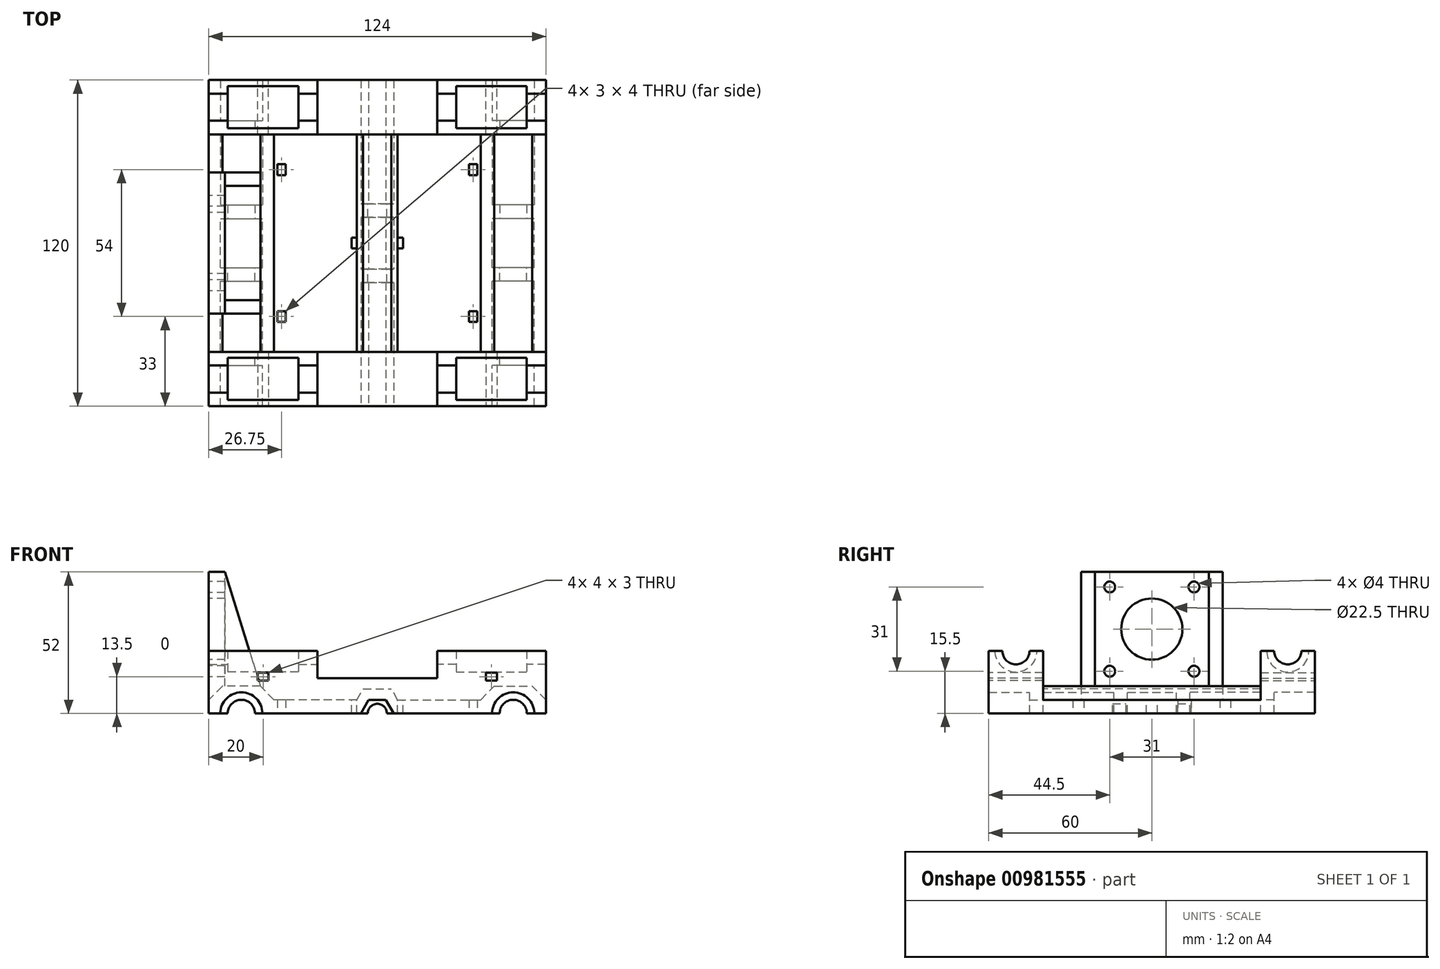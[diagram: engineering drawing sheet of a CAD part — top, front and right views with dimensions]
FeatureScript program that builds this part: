
annotation { "Feature Type Name" : "Feature", "Feature Type Description" : "" }
export const myFeature = defineFeature(function(context is Context, id is Id, definition is map)
    precondition{}
    {
        {
            var Q0;
            Q0=qCreatedBy(makeId("Front.planeOp"),FACE);
            var sketch = newSketch(context, id + "F0", { "sketchPlane" : qUnion([Q0])});
            skLineSegment(sketch, "E0", {"start": v(0, 0) * mm, "end": v(-42.25, 0) * mm});
            skArc(sketch, "E1", {"start": v(-42.25, 0) * mm, "mid": v(-50, 7.75) * mm, "end": v(-57.75, 0) * mm});
            skLineSegment(sketch, "E2", {"start": v(-57.75, 0) * mm, "end": v(-62, 0) * mm});
            skLineSegment(sketch, "E3", {"start": v(-43, 10) * mm, "end": v(-38, 5) * mm});
            skLineSegment(sketch, "E4", {"start": v(-38, 5) * mm, "end": v(0, 5) * mm});
            skLineSegment(sketch, "E5", {"start": v(-57, 10) * mm, "end": v(-43, 10) * mm});
            skLineSegment(sketch, "E6", {"start": v(-57, 10) * mm, "end": v(-62, 5) * mm});
            skLineSegment(sketch, "E7", {"start": v(-62, 5) * mm, "end": v(-62, 0) * mm});
            skLineSegment(sketch, "E8", {"start": v(0, 0) * mm, "end": v(0, 5) * mm});
            skSolve(sketch);
        }
        {
            var Q0;
            Q0=makeQuery(id+"F0.imprint","IMPRINT",FACE,{"disambiguationData":[TD([[makeQuery(id+"F0.imprint","IMPRINT",EDGE,{"derivedFrom":sQuery(id+"F0.wireOp",EDGE,"E0")}),-1.0]])]});
            extrude(context, id + "F1", {"entities" : qUnion([Q0]), "endBound" : BoundingType.SYMMETRIC, "depth" : 120 * mm, "offsetDistance" : 25 * mm});
        }
        {
            var Q0;
            Q0=makeQuery(id+"F1.opExtrude","SWEPT_BODY",BODY,{"disambiguationData":[OSD([sQuery(id+"F0.wireOp",EDGE,"E0"),sQuery(id+"F0.wireOp",EDGE,"E1"),sQuery(id+"F0.wireOp",EDGE,"E2"),sQuery(id+"F0.wireOp",EDGE,"E3"),sQuery(id+"F0.wireOp",EDGE,"E4"),sQuery(id+"F0.wireOp",EDGE,"E5"),sQuery(id+"F0.wireOp",EDGE,"E6"),sQuery(id+"F0.wireOp",EDGE,"E7"),sQuery(id+"F0.wireOp",EDGE,"E8")])]});
            var Q1;
            Q1=qCreatedBy(makeId("Right.planeOp"),FACE);
            mirror(context, id + "F2", {"operationType" : NewBodyOperationType.ADD, "entities" : qUnion([Q0]), "mirrorPlane" : qUnion([Q1])});
        }
        {
            var Q0;
            {var subQ0=makeQuery(id+"F1.opExtrude","CAP_FACE",FACE,{"disambiguationData":[OSD([sQuery(id+"F0.wireOp",EDGE,"E0"),sQuery(id+"F0.wireOp",EDGE,"E1"),sQuery(id+"F0.wireOp",EDGE,"E2"),sQuery(id+"F0.wireOp",EDGE,"E3"),sQuery(id+"F0.wireOp",EDGE,"E4"),sQuery(id+"F0.wireOp",EDGE,"E5"),sQuery(id+"F0.wireOp",EDGE,"E6"),sQuery(id+"F0.wireOp",EDGE,"E7"),sQuery(id+"F0.wireOp",EDGE,"E8")])],"isStart":false});Q0=makeQuery(id+"F2.boolean.opBoolean","MERGE",FACE,{"derivedFrom":[subQ0,makeQuery(id+"F2.opPattern","COPY",FACE,{"derivedFrom":subQ0,"instanceName":"1"})]});}
            var sketch = newSketch(context, id + "F3", { "sketchPlane" : qUnion([Q0])});
            skCircle(sketch, "E9.cCircle", {"center": v(0, 0) * mm, "radius": 5.25 * mm, "construction": true});
            skLineSegment(sketch, "E9.0", {"start": v(-3.03, 5.25) * mm, "end": v(3.03, 5.25) * mm});
            skLineSegment(sketch, "E9.1", {"start": v(3.03, 5.25) * mm, "end": v(6.06, 0) * mm});
            skLineSegment(sketch, "E9.2", {"start": v(6.06, 0) * mm, "end": v(3.03, -5.25) * mm});
            skLineSegment(sketch, "E9.3", {"start": v(3.03, -5.25) * mm, "end": v(-3.03, -5.25) * mm});
            skLineSegment(sketch, "E9.4", {"start": v(-3.03, -5.25) * mm, "end": v(-6.06, 0) * mm});
            skLineSegment(sketch, "E9.5", {"start": v(-6.06, 0) * mm, "end": v(-3.03, 5.25) * mm});
            skPoint(sketch, "E9.0.midPoint", {"position": v(0, 5.25) * mm});
            skCircle(sketch, "E10.cCircle", {"center": v(0, 0) * mm, "radius": 9 * mm, "construction": true});
            skLineSegment(sketch, "E10.0", {"start": v(-5.2, 9) * mm, "end": v(5.2, 9) * mm});
            skLineSegment(sketch, "E10.1", {"start": v(5.2, 9) * mm, "end": v(10.4, 0) * mm});
            skLineSegment(sketch, "E10.2", {"start": v(10.4, 0) * mm, "end": v(5.2, -9) * mm});
            skLineSegment(sketch, "E10.3", {"start": v(5.2, -9) * mm, "end": v(-5.2, -9) * mm});
            skLineSegment(sketch, "E10.4", {"start": v(-5.2, -9) * mm, "end": v(-10.4, 0) * mm});
            skLineSegment(sketch, "E10.5", {"start": v(-10.4, 0) * mm, "end": v(-5.2, 9) * mm});
            skPoint(sketch, "E10.0.midPoint", {"position": v(0, 9) * mm});
            skLineSegment(sketch, "E11", {"start": v(-10.4, 0) * mm, "end": v(10.4, 0) * mm});
            skSolve(sketch);
        }
        {
            var Q0;
            {var subQ0=sQuery(id+"F3.wireOp",EDGE,"E11");var subQ1=sQuery(id+"F3.wireOp",EDGE,"E9.5");var subQ2=makeQuery(id+"F3.imprint","INTERSECT",VERTEX,{"derivedFrom":[sQuery(id+"F3.wireOp",EDGE,"E9.4"),subQ1,subQ0]});Q0=makeQuery(id+"F3.imprint","IMPRINT",FACE,{"disambiguationData":[TD([[makeQuery(id+"F3.imprint","IMPRINT",EDGE,{"disambiguationData":[TD([[subQ2,-1.0]])],"derivedFrom":subQ1}),1.0]])]});}
            var Q1;
            {var subQ2=sQuery(id+"F3.wireOp",EDGE,"E9.0");Q1=makeQuery(id+"F3.imprint","IMPRINT",FACE,{"disambiguationData":[TD([[makeQuery(id+"F3.imprint","IMPRINT",EDGE,{"derivedFrom":subQ2}),1.0]])]});}
            var Q2;
            {var subQ0=sQuery(id+"F3.wireOp",EDGE,"E11");var subQ1=sQuery(id+"F3.wireOp",EDGE,"E9.1");var subQ2=makeQuery(id+"F3.imprint","INTERSECT",VERTEX,{"derivedFrom":[subQ1,sQuery(id+"F3.wireOp",EDGE,"E9.2"),subQ0]});Q2=makeQuery(id+"F3.imprint","IMPRINT",FACE,{"disambiguationData":[TD([[makeQuery(id+"F3.imprint","IMPRINT",EDGE,{"disambiguationData":[TD([[subQ2,1.0]])],"derivedFrom":subQ1}),1.0]])]});}
            var Q3;
            {var subQ0=sQuery(id+"F3.wireOp",EDGE,"E9.0");Q3=makeQuery(id+"F3.imprint","IMPRINT",FACE,{"disambiguationData":[TD([[makeQuery(id+"F3.imprint","IMPRINT",EDGE,{"derivedFrom":subQ0}),-1.0]])]});}
            var Q4;
            {var subQ0=makeQuery(id+"F1.opExtrude","CAP_FACE",FACE,{"disambiguationData":[OSD([sQuery(id+"F0.wireOp",EDGE,"E0"),sQuery(id+"F0.wireOp",EDGE,"E1"),sQuery(id+"F0.wireOp",EDGE,"E2"),sQuery(id+"F0.wireOp",EDGE,"E3"),sQuery(id+"F0.wireOp",EDGE,"E4"),sQuery(id+"F0.wireOp",EDGE,"E5"),sQuery(id+"F0.wireOp",EDGE,"E6"),sQuery(id+"F0.wireOp",EDGE,"E7"),sQuery(id+"F0.wireOp",EDGE,"E8")])],"isStart":true});Q4=makeQuery(id+"F2.boolean.opBoolean","MERGE",FACE,{"derivedFrom":[subQ0,makeQuery(id+"F2.opPattern","COPY",FACE,{"derivedFrom":subQ0,"instanceName":"1"})]});}
            extrude(context, id + "F4", {"entities" : qUnion([Q0, Q1, Q2, Q3]), "operationType" : NewBodyOperationType.ADD, "endBound" : BoundingType.UP_TO_SURFACE, "oppositeDirection" : true, "depth" : 123.9 * mm, "endBoundEntityFace" : qUnion([Q4]), "offsetDistance" : 25 * mm});
        }
        {
            var Q0;
            {var subQ0=sQuery(id+"F3.wireOp",EDGE,"E11");var subQ1=sQuery(id+"F3.wireOp",EDGE,"E9.1");var subQ2=makeQuery(id+"F3.imprint","INTERSECT",VERTEX,{"derivedFrom":[subQ1,sQuery(id+"F3.wireOp",EDGE,"E9.2"),subQ0]});Q0=makeQuery(id+"F3.imprint","IMPRINT",FACE,{"disambiguationData":[TD([[makeQuery(id+"F3.imprint","IMPRINT",EDGE,{"disambiguationData":[TD([[subQ2,1.0]])],"derivedFrom":subQ1}),-1.0]])]});}
            extrude(context, id + "F5", {"entities" : qUnion([Q0]), "operationType" : NewBodyOperationType.REMOVE, "endBound" : BoundingType.THROUGH_ALL, "oppositeDirection" : true, "depth" : 25 * mm, "offsetDistance" : 25 * mm});
        }
        {
            var Q0;
            Q0=makeQuery(id+"F1.opExtrude","SWEPT_FACE",FACE,{"disambiguationData":[OSD([sQuery(id+"F0.wireOp",EDGE,"E5")])]});
            var sketch = newSketch(context, id + "F6", { "sketchPlane" : qUnion([Q0])});
            skLineSegment(sketch, "E12.bottom", {"start": v(62, -40) * mm, "end": v(-62, -40) * mm});
            skLineSegment(sketch, "E12.top", {"start": v(62, -60) * mm, "end": v(-62, -60) * mm});
            skLineSegment(sketch, "E12.left", {"start": v(62, -40) * mm, "end": v(62, -60) * mm});
            skLineSegment(sketch, "E12.right", {"start": v(-62, -40) * mm, "end": v(-62, -60) * mm});
            skPoint(sketch, "E12.middle", {"position": v(0, -50) * mm});
            skSolve(sketch);
        }
        {
            var Q0;
            {var subQ0=sQuery(id+"F6.wireOp",EDGE,"E12.right");Q0=makeQuery(id+"F6.imprint","IMPRINT",FACE,{"disambiguationData":[TD([[makeQuery(id+"F6.imprint","IMPRINT",EDGE,{"derivedFrom":subQ0}),1.0]])]});}
            var Q1;
            {var subQ0=sQuery(id+"F6.wireOp",EDGE,"E12.bottom");var subQ1=sQuery(id+"F0.wireOp",EDGE,"E5");var subQ2=makeQuery(id+"F1.opExtrude","SWEPT_EDGE",EDGE,{"disambiguationData":[OSD([sQuery(id+"F0.wireOp",EDGE,"E3"),subQ1])]});var subQ3=makeQuery(id+"F6.imprint","INTERSECT",VERTEX,{"derivedFrom":[subQ2,subQ0]});Q1=makeQuery(id+"F6.imprint","IMPRINT",FACE,{"disambiguationData":[TD([[makeQuery(id+"F6.imprint","IMPRINT",EDGE,{"disambiguationData":[TD([[subQ3,-1.0]])],"derivedFrom":subQ0}),1.0]])]});}
            var Q2;
            {var subQ0=sQuery(id+"F6.wireOp",EDGE,"E12.left");Q2=makeQuery(id+"F6.imprint","IMPRINT",FACE,{"disambiguationData":[TD([[makeQuery(id+"F6.imprint","IMPRINT",EDGE,{"derivedFrom":subQ0}),-1.0]])]});}
            var Q3;
            {var subQ1=sQuery(id+"F0.wireOp",EDGE,"E5");var subQ6=makeQuery(id+"F1.opExtrude","CAP_EDGE",EDGE,{"disambiguationData":[OSD([subQ1])],"isStart":true});Q3=makeQuery(id+"F6.imprint","IMPRINT",FACE,{"disambiguationData":[TD([[makeQuery(id+"F6.imprint","IMPRINT",EDGE,{"derivedFrom":subQ6}),-1.0]])]});}
            var Q4;
            Q4=makeQuery(id+"F1.opExtrude","SWEPT_BODY",BODY,{"disambiguationData":[OSD([sQuery(id+"F0.wireOp",EDGE,"E0"),sQuery(id+"F0.wireOp",EDGE,"E1"),sQuery(id+"F0.wireOp",EDGE,"E2"),sQuery(id+"F0.wireOp",EDGE,"E3"),sQuery(id+"F0.wireOp",EDGE,"E4"),sQuery(id+"F0.wireOp",EDGE,"E5"),sQuery(id+"F0.wireOp",EDGE,"E6"),sQuery(id+"F0.wireOp",EDGE,"E7"),sQuery(id+"F0.wireOp",EDGE,"E8")])]});
            extrude(context, id + "F7", {"entities" : qUnion([Q0, Q1, Q2, Q3]), "operationType" : NewBodyOperationType.ADD, "endBound" : BoundingType.UP_TO_BODY, "oppositeDirection" : true, "depth" : 25 * mm, "endBoundEntityBody" : qUnion([Q4]), "offsetDistance" : 25 * mm});
        }
        {
            var Q0;
            Q0 = qSketchRegion(id + "F6", true);
            extrude(context, id + "F8", {"entities" : qUnion([Q0]), "operationType" : NewBodyOperationType.ADD, "depth" : 3 * mm, "offsetDistance" : 25 * mm});
        }
        {
            var Q0;
            {var subQ0=sQuery(id+"F6.wireOp",EDGE,"E12.right");Q0=makeQuery(id+"F8.boolean.opBoolean","MERGE",FACE,{"derivedFrom":[makeQuery(id+"F7.boolean.opBoolean","MERGE",FACE,{"derivedFrom":[makeQuery(id+"F1.opExtrude","SWEPT_FACE",FACE,{"disambiguationData":[OSD([sQuery(id+"F0.wireOp",EDGE,"E7")])]}),makeQuery(id+"F7.opExtrude","SWEPT_FACE",FACE,{"disambiguationData":[OSD([subQ0])]})]}),makeQuery(id+"F8.opExtrude","SWEPT_FACE",FACE,{"disambiguationData":[OSD([subQ0])]})]});}
            var sketch = newSketch(context, id + "F9", { "sketchPlane" : qUnion([Q0])});
            skLineSegment(sketch, "E13", {"start": v(50, 13) * mm, "end": v(50, 23) * mm, "construction": true});
            skArc(sketch, "E14", {"start": v(42.25, 23) * mm, "mid": v(44.52, 17.52) * mm, "end": v(50, 15.25) * mm});
            skLineSegment(sketch, "E15", {"start": v(50, 23) * mm, "end": v(40, 23) * mm, "construction": true});
            skLineSegment(sketch, "E16", {"start": v(40, 23) * mm, "end": v(40, 13) * mm});
            skLineSegment(sketch, "E17", {"start": v(42.25, 23) * mm, "end": v(40, 23) * mm});
            skLineSegment(sketch, "E18", {"start": v(50, 15.25) * mm, "end": v(50, 13) * mm});
            skLineSegment(sketch, "E19.MirrorCS", {"start": v(57.75, 23) * mm, "end": v(60, 23) * mm});
            skLineSegment(sketch, "E20.MirrorCS", {"start": v(50, 23) * mm, "end": v(60, 23) * mm, "construction": true});
            skArc(sketch, "E21.MirrorCS", {"start": v(57.75, 23) * mm, "mid": v(55.48, 17.52) * mm, "end": v(50, 15.25) * mm});
            skLineSegment(sketch, "E22.MirrorCS", {"start": v(60, 23) * mm, "end": v(60, 13) * mm});
            skLineSegment(sketch, "E23", {"start": v(40, 13) * mm, "end": v(60, 13) * mm});
            skSolve(sketch);
        }
        {
            var Q0;
            Q0 = qSketchRegion(id + "F9", true);
            extrude(context, id + "F10", {"entities" : qUnion([Q0]), "operationType" : NewBodyOperationType.ADD, "oppositeDirection" : true, "depth" : 40 * mm, "offsetDistance" : 25 * mm});
        }
        {
            var Q0;
            {var subQ0=sQuery(id+"F6.wireOp",EDGE,"E12.right");Q0=makeQuery(id+"F10.boolean.opBoolean","MERGE",FACE,{"derivedFrom":[makeQuery(id+"F8.boolean.opBoolean","MERGE",FACE,{"derivedFrom":[makeQuery(id+"F7.boolean.opBoolean","MERGE",FACE,{"derivedFrom":[makeQuery(id+"F1.opExtrude","SWEPT_FACE",FACE,{"disambiguationData":[OSD([sQuery(id+"F0.wireOp",EDGE,"E7")])]}),makeQuery(id+"F7.opExtrude","SWEPT_FACE",FACE,{"disambiguationData":[OSD([subQ0])]})]}),makeQuery(id+"F8.opExtrude","SWEPT_FACE",FACE,{"disambiguationData":[OSD([subQ0])]})]}),makeQuery(id+"F10.opExtrude","CAP_FACE",FACE,{"disambiguationData":[OSD([sQuery(id+"F9.wireOp",EDGE,"E14"),sQuery(id+"F9.wireOp",EDGE,"E16"),sQuery(id+"F9.wireOp",EDGE,"E17"),sQuery(id+"F9.wireOp",EDGE,"E21.MirrorCS"),sQuery(id+"F9.wireOp",EDGE,"E19.MirrorCS"),sQuery(id+"F9.wireOp",EDGE,"E22.MirrorCS"),sQuery(id+"F9.wireOp",EDGE,"E23")])],"isStart":true})]});}
            var sketch = newSketch(context, id + "F11", { "sketchPlane" : qUnion([Q0])});
            skLineSegment(sketch, "E24", {"start": v(42.25, 23) * mm, "end": v(57.75, 23) * mm});
            skSolve(sketch);
        }
        {
            var Q0;
            Q0=makeQuery(id+"F11.imprint","IMPRINT",FACE,{"disambiguationData":[TD([[makeQuery(id+"F11.imprint","IMPRINT",EDGE,{"derivedFrom":sQuery(id+"F11.wireOp",EDGE,"E24")}),-1.0]])]});
            extrude(context, id + "F12", {"entities" : qUnion([Q0]), "operationType" : NewBodyOperationType.ADD, "oppositeDirection" : true, "depth" : 7 * mm, "offsetDistance" : 25 * mm});
        }
        {
            var Q0;
            Q0=makeQuery(id+"F10.opExtrude","CAP_FACE",FACE,{"disambiguationData":[OSD([sQuery(id+"F9.wireOp",EDGE,"E14"),sQuery(id+"F9.wireOp",EDGE,"E16"),sQuery(id+"F9.wireOp",EDGE,"E17"),sQuery(id+"F9.wireOp",EDGE,"E21.MirrorCS"),sQuery(id+"F9.wireOp",EDGE,"E19.MirrorCS"),sQuery(id+"F9.wireOp",EDGE,"E22.MirrorCS"),sQuery(id+"F9.wireOp",EDGE,"E23")])],"isStart":false});
            var sketch = newSketch(context, id + "F13", { "sketchPlane" : qUnion([Q0])});
            skLineSegment(sketch, "E25", {"start": v(-57.75, 23) * mm, "end": v(-42.25, 23) * mm});
            skSolve(sketch);
        }
        {
            var Q0;
            Q0=makeQuery(id+"F13.imprint","IMPRINT",FACE,{"disambiguationData":[TD([[makeQuery(id+"F13.imprint","IMPRINT",EDGE,{"derivedFrom":sQuery(id+"F13.wireOp",EDGE,"E25")}),-1.0]])]});
            extrude(context, id + "F14", {"entities" : qUnion([Q0]), "operationType" : NewBodyOperationType.ADD, "oppositeDirection" : true, "depth" : 7 * mm, "offsetDistance" : 25 * mm});
        }
        {
            var Q0;
            Q0=makeQuery(id+"F12.opExtrude","CAP_FACE",FACE,{"disambiguationData":[OSD([sQuery(id+"F9.wireOp",EDGE,"E14"),sQuery(id+"F9.wireOp",EDGE,"E21.MirrorCS"),sQuery(id+"F11.wireOp",EDGE,"E24")])],"isStart":false});
            var sketch = newSketch(context, id + "F15", { "sketchPlane" : qUnion([Q0])});
            skCircle(sketch, "E26", {"center": v(-50, 23) * mm, "radius": 5 * mm});
            skSolve(sketch);
        }
        {
            var Q0;
            Q0 = qSketchRegion(id + "F15", true);
            extrude(context, id + "F16", {"entities" : qUnion([Q0]), "operationType" : NewBodyOperationType.REMOVE, "endBound" : BoundingType.SYMMETRIC, "oppositeDirection" : true, "depth" : 100 * mm, "offsetDistance" : 25 * mm});
        }
        {
            var Q0;
            {var subQ0=sQuery(id+"F0.wireOp",EDGE,"E1");var subQ8=sQuery(id+"F0.wireOp",EDGE,"E0");var subQ17=makeQuery(id+"F1.opExtrude","SWEPT_FACE",FACE,{"disambiguationData":[OSD([subQ8])]});Q0=makeQuery(id+"F5.boolean.opBoolean","SPLIT",FACE,{"disambiguationData":[TD([makeQuery(id+"F1.opExtrude","SWEPT_FACE",FACE,{"disambiguationData":[OSD([subQ0])]})])],"derivedFrom":makeQuery(id+"F2.boolean.opBoolean","MERGE",FACE,{"derivedFrom":[subQ17,makeQuery(id+"F2.opPattern","COPY",FACE,{"derivedFrom":subQ17,"instanceName":"1"})]})});}
            var sketch = newSketch(context, id + "F17", { "sketchPlane" : qUnion([Q0])});
            skLineSegment(sketch, "E27.bottom", {"start": v(-57.75, 45) * mm, "end": v(-42.25, 45) * mm});
            skLineSegment(sketch, "E27.top", {"start": v(-57.75, 40) * mm, "end": v(-42.25, 40) * mm});
            skLineSegment(sketch, "E27.left", {"start": v(-57.75, 45) * mm, "end": v(-57.75, 40) * mm});
            skLineSegment(sketch, "E27.right", {"start": v(-42.25, 45) * mm, "end": v(-42.25, 40) * mm});
            skLineSegment(sketch, "E28.bottom", {"start": v(-57.75, 14) * mm, "end": v(-42.25, 14) * mm});
            skLineSegment(sketch, "E28.top", {"start": v(-57.75, 9) * mm, "end": v(-42.25, 9) * mm});
            skLineSegment(sketch, "E28.left", {"start": v(-57.75, 14) * mm, "end": v(-57.75, 9) * mm});
            skLineSegment(sketch, "E28.right", {"start": v(-42.25, 14) * mm, "end": v(-42.25, 9) * mm});
            skSolve(sketch);
        }
        {
            var Q0;
            Q0 = qSketchRegion(id + "F17", true);
            var Q1;
            Q1=makeQuery(id+"F1.opExtrude","SWEPT_FACE",FACE,{"disambiguationData":[OSD([sQuery(id+"F0.wireOp",EDGE,"E1")])]});
            var Q2;
            Q2=makeQuery(id+"F1.opExtrude","SWEPT_BODY",BODY,{"disambiguationData":[OSD([sQuery(id+"F0.wireOp",EDGE,"E0"),sQuery(id+"F0.wireOp",EDGE,"E1"),sQuery(id+"F0.wireOp",EDGE,"E2"),sQuery(id+"F0.wireOp",EDGE,"E3"),sQuery(id+"F0.wireOp",EDGE,"E4"),sQuery(id+"F0.wireOp",EDGE,"E5"),sQuery(id+"F0.wireOp",EDGE,"E6"),sQuery(id+"F0.wireOp",EDGE,"E7"),sQuery(id+"F0.wireOp",EDGE,"E8")])]});
            extrude(context, id + "F18", {"entities" : qUnion([Q0]), "operationType" : NewBodyOperationType.ADD, "endBound" : BoundingType.UP_TO_SURFACE, "oppositeDirection" : true, "depth" : 25 * mm, "endBoundEntityFace" : qUnion([Q1]), "endBoundEntityBody" : qUnion([Q2]), "offsetDistance" : 25 * mm});
        }
        {
            var Q0;
            Q0=makeQuery(id+"F18.opExtrude","SWEPT_FACE",FACE,{"disambiguationData":[OSD([sQuery(id+"F17.wireOp",EDGE,"E28.top")])]});
            var sketch = newSketch(context, id + "F19", { "sketchPlane" : qUnion([Q0])});
            skCircle(sketch, "E29", {"center": v(50, 0) * mm, "radius": 5 * mm});
            skSolve(sketch);
        }
        {
            var Q0;
            Q0 = qSketchRegion(id + "F19", true);
            extrude(context, id + "F20", {"entities" : qUnion([Q0]), "operationType" : NewBodyOperationType.REMOVE, "endBound" : BoundingType.THROUGH_ALL, "oppositeDirection" : true, "depth" : 25 * mm, "offsetDistance" : 25 * mm});
        }
        {
            var Q0;
            {var subQ0=sQuery(id+"F6.wireOp",EDGE,"E12.top");var subQ1=sQuery(id+"F0.wireOp",EDGE,"E4");var subQ2=makeQuery(id+"F1.opExtrude","CAP_FACE",FACE,{"disambiguationData":[OSD([sQuery(id+"F0.wireOp",EDGE,"E0"),sQuery(id+"F0.wireOp",EDGE,"E1"),sQuery(id+"F0.wireOp",EDGE,"E2"),sQuery(id+"F0.wireOp",EDGE,"E3"),subQ1,sQuery(id+"F0.wireOp",EDGE,"E5"),sQuery(id+"F0.wireOp",EDGE,"E6"),sQuery(id+"F0.wireOp",EDGE,"E7"),sQuery(id+"F0.wireOp",EDGE,"E8")])],"isStart":false});Q0=makeQuery(id+"F10.boolean.opBoolean","MERGE",FACE,{"derivedFrom":[makeQuery(id+"F8.boolean.opBoolean","MERGE",FACE,{"derivedFrom":[makeQuery(id+"F7.boolean.opBoolean","MERGE",FACE,{"derivedFrom":[makeQuery(id+"F4.boolean.opBoolean","MERGE",FACE,{"derivedFrom":[makeQuery(id+"F2.boolean.opBoolean","MERGE",FACE,{"derivedFrom":[subQ2,makeQuery(id+"F2.opPattern","COPY",FACE,{"derivedFrom":subQ2,"instanceName":"1"})]}),makeQuery(id+"F4.opExtrude","CAP_FACE",FACE,{"disambiguationData":[OSD([subQ1,sQuery(id+"F3.wireOp",EDGE,"E9.1"),sQuery(id+"F3.wireOp",EDGE,"E9.5"),sQuery(id+"F3.wireOp",EDGE,"E10.0"),sQuery(id+"F3.wireOp",EDGE,"E10.1"),sQuery(id+"F3.wireOp",EDGE,"E10.5"),sQuery(id+"F3.wireOp",EDGE,"E11")])],"isStart":true})]}),makeQuery(id+"F7.opExtrude","SWEPT_FACE",FACE,{"disambiguationData":[OSD([subQ0])]})]}),makeQuery(id+"F8.opExtrude","SWEPT_FACE",FACE,{"disambiguationData":[OSD([subQ0])]})]}),makeQuery(id+"F10.opExtrude","SWEPT_FACE",FACE,{"disambiguationData":[OSD([sQuery(id+"F9.wireOp",EDGE,"E22.MirrorCS")])]})]});}
            var sketch = newSketch(context, id + "F21", { "sketchPlane" : qUnion([Q0])});
            skLineSegment(sketch, "E30", {"start": v(-42, 23) * mm, "end": v(-42, 13.5) * mm, "construction": true});
            skLineSegment(sketch, "E31.bottom", {"start": v(-40, 12) * mm, "end": v(-44, 12) * mm});
            skLineSegment(sketch, "E31.top", {"start": v(-40, 15) * mm, "end": v(-44, 15) * mm});
            skLineSegment(sketch, "E31.left", {"start": v(-40, 12) * mm, "end": v(-40, 15) * mm});
            skLineSegment(sketch, "E31.right", {"start": v(-44, 12) * mm, "end": v(-44, 15) * mm});
            skPoint(sketch, "E31.middle", {"position": v(-42, 13.5) * mm});
            skSolve(sketch);
        }
        {
            var Q0;
            Q0=makeQuery(id+"F21.imprint","IMPRINT",FACE,{"disambiguationData":[TD([[makeQuery(id+"F21.imprint","IMPRINT",EDGE,{"derivedFrom":sQuery(id+"F21.wireOp",EDGE,"E31.bottom")}),-1.0]])]});
            extrude(context, id + "F22", {"entities" : qUnion([Q0]), "operationType" : NewBodyOperationType.REMOVE, "endBound" : BoundingType.THROUGH_ALL, "oppositeDirection" : true, "depth" : 25 * mm, "offsetDistance" : 25 * mm});
        }
        {
            var Q0;
            {var subQ1=sQuery(id+"F17.wireOp",EDGE,"E28.top");var subQ2=sQuery(id+"F3.wireOp",EDGE,"E9.5");var subQ3=makeQuery(id+"F5.opExtrude","SWEPT_FACE",FACE,{"disambiguationData":[OSD([subQ2])]});var subQ16=sQuery(id+"F0.wireOp",EDGE,"E2");var subQ17=sQuery(id+"F0.wireOp",EDGE,"E1");var subQ18=sQuery(id+"F0.wireOp",EDGE,"E0");var subQ20=sQuery(id+"F17.wireOp",EDGE,"E27.top");var subQ24=sQuery(id+"F17.wireOp",EDGE,"E28.bottom");var subQ26=makeQuery(id+"F1.opExtrude","SWEPT_FACE",FACE,{"disambiguationData":[OSD([subQ17])]});var subQ27=sQuery(id+"F17.wireOp",EDGE,"E27.bottom");var subQ28=makeQuery(id+"F1.opExtrude","SWEPT_FACE",FACE,{"disambiguationData":[OSD([subQ18])]});Q0=makeQuery(id+"F20.boolean.opBoolean","SPLIT",FACE,{"disambiguationData":[TD([makeQuery(id+"F5.boolean.opBoolean","COPY",FACE,{"derivedFrom":subQ3})])],"derivedFrom":makeQuery(id+"F18.boolean.opBoolean","MERGE",FACE,{"derivedFrom":[makeQuery(id+"F1.opExtrude","SWEPT_FACE",FACE,{"disambiguationData":[OSD([subQ16])]}),makeQuery(id+"F5.boolean.opBoolean","SPLIT",FACE,{"disambiguationData":[TD([subQ26])],"derivedFrom":makeQuery(id+"F2.boolean.opBoolean","MERGE",FACE,{"derivedFrom":[subQ28,makeQuery(id+"F2.opPattern","COPY",FACE,{"derivedFrom":subQ28,"instanceName":"1"})]})}),makeQuery(id+"F18.opExtrude","CAP_FACE",FACE,{"disambiguationData":[OSD([subQ27,subQ20,sQuery(id+"F17.wireOp",EDGE,"E27.left"),sQuery(id+"F17.wireOp",EDGE,"E27.right")])],"isStart":true}),makeQuery(id+"F18.opExtrude","CAP_FACE",FACE,{"disambiguationData":[OSD([subQ24,subQ1,sQuery(id+"F17.wireOp",EDGE,"E28.left"),sQuery(id+"F17.wireOp",EDGE,"E28.right")])],"isStart":true})]})});}
            var sketch = newSketch(context, id + "F23", { "sketchPlane" : qUnion([Q0])});
            skLineSegment(sketch, "E32", {"start": v(-42.25, 27) * mm, "end": v(-35.25, 27) * mm, "construction": true});
            skLineSegment(sketch, "E33.bottom", {"start": v(-36.75, 29) * mm, "end": v(-33.75, 29) * mm});
            skLineSegment(sketch, "E33.top", {"start": v(-36.75, 25) * mm, "end": v(-33.75, 25) * mm});
            skLineSegment(sketch, "E33.left", {"start": v(-36.75, 29) * mm, "end": v(-36.75, 25) * mm});
            skLineSegment(sketch, "E33.right", {"start": v(-33.75, 29) * mm, "end": v(-33.75, 25) * mm});
            skPoint(sketch, "E33.middle", {"position": v(-35.25, 27) * mm});
            skSolve(sketch);
        }
        {
            var Q0;
            Q0=makeQuery(id+"F23.imprint","IMPRINT",FACE,{"disambiguationData":[TD([[makeQuery(id+"F23.imprint","IMPRINT",EDGE,{"derivedFrom":sQuery(id+"F23.wireOp",EDGE,"E33.bottom")}),-1.0]])]});
            var Q1;
            Q1=sQuery(id+"F23.wireOp",EDGE,"E33.top");
            var Q2;
            Q2=sQuery(id+"F23.wireOp",EDGE,"E33.right");
            var Q3;
            Q3=sQuery(id+"F23.wireOp",EDGE,"E33.bottom");
            var Q4;
            Q4=sQuery(id+"F23.wireOp",EDGE,"E33.left");
            extrude(context, id + "F24", {"entities" : qUnion([Q0]), "operationType" : NewBodyOperationType.REMOVE, "surfaceEntities" : qUnion([Q1, Q2, Q3, Q4]), "endBound" : BoundingType.THROUGH_ALL, "oppositeDirection" : true, "depth" : 25 * mm, "offsetDistance" : 25 * mm});
        }
        {
            var Q0;
            Q0=qCreatedBy(makeId("Top.planeOp"),FACE);
            var sketch = newSketch(context, id + "F25", { "sketchPlane" : qUnion([Q0])});
            skLineSegment(sketch, "E34", {"start": v(-62, 0) * mm, "end": v(0, 0) * mm});
            skLineSegment(sketch, "E35", {"start": v(0, 0) * mm, "end": v(0, -60) * mm});
            skLineSegment(sketch, "E36", {"start": v(0, -60) * mm, "end": v(62, -60) * mm});
            skLineSegment(sketch, "E37", {"start": v(62, -60) * mm, "end": v(62, 60) * mm});
            skLineSegment(sketch, "E38", {"start": v(62, 60) * mm, "end": v(-62, 60) * mm});
            skLineSegment(sketch, "E39", {"start": v(-62, 60) * mm, "end": v(-62, 0) * mm});
            skSolve(sketch);
        }
        {
            var Q0;
            Q0 = qSketchRegion(id + "F25", true);
            extrude(context, id + "F26", {"entities" : qUnion([Q0]), "operationType" : NewBodyOperationType.REMOVE, "endBound" : BoundingType.THROUGH_ALL, "depth" : 25 * mm, "offsetDistance" : 25 * mm});
        }
        {
            var Q0;
            Q0=makeQuery(id+"F1.opExtrude","SWEPT_BODY",BODY,{"disambiguationData":[OSD([sQuery(id+"F0.wireOp",EDGE,"E0"),sQuery(id+"F0.wireOp",EDGE,"E1"),sQuery(id+"F0.wireOp",EDGE,"E2"),sQuery(id+"F0.wireOp",EDGE,"E3"),sQuery(id+"F0.wireOp",EDGE,"E4"),sQuery(id+"F0.wireOp",EDGE,"E5"),sQuery(id+"F0.wireOp",EDGE,"E6"),sQuery(id+"F0.wireOp",EDGE,"E7"),sQuery(id+"F0.wireOp",EDGE,"E8")])]});
            var Q1;
            Q1=makeQuery(id+"F26.boolean.opBoolean","COPY",FACE,{"derivedFrom":makeQuery(id+"F26.opExtrude","SWEPT_FACE",FACE,{"disambiguationData":[OSD([sQuery(id+"F25.wireOp",EDGE,"E35")])]})});
            mirror(context, id + "F27", {"operationType" : NewBodyOperationType.ADD, "entities" : qUnion([Q0]), "mirrorPlane" : qUnion([Q1])});
        }
        {
            var Q0;
            Q0=makeQuery(id+"F1.opExtrude","SWEPT_BODY",BODY,{"disambiguationData":[OSD([sQuery(id+"F0.wireOp",EDGE,"E0"),sQuery(id+"F0.wireOp",EDGE,"E1"),sQuery(id+"F0.wireOp",EDGE,"E2"),sQuery(id+"F0.wireOp",EDGE,"E3"),sQuery(id+"F0.wireOp",EDGE,"E4"),sQuery(id+"F0.wireOp",EDGE,"E5"),sQuery(id+"F0.wireOp",EDGE,"E6"),sQuery(id+"F0.wireOp",EDGE,"E7"),sQuery(id+"F0.wireOp",EDGE,"E8")])]});
            var Q1;
            Q1=makeQuery(id+"F0.imprint","IMPRINT",FACE,{"disambiguationData":[TD([[makeQuery(id+"F0.imprint","IMPRINT",EDGE,{"derivedFrom":sQuery(id+"F0.wireOp",EDGE,"E0")}),-1.0]])]});
            mirror(context, id + "F28", {"operationType" : NewBodyOperationType.ADD, "entities" : qUnion([Q0]), "mirrorPlane" : qUnion([Q1])});
        }
        {
            var Q0;
            {var subQ0=sQuery(id+"F9.wireOp",EDGE,"E21.MirrorCS");var subQ1=sQuery(id+"F9.wireOp",EDGE,"E14");var subQ2=sQuery(id+"F6.wireOp",EDGE,"E12.right");var subQ3=makeQuery(id+"F12.boolean.opBoolean","MERGE",FACE,{"derivedFrom":[makeQuery(id+"F10.boolean.opBoolean","MERGE",FACE,{"derivedFrom":[makeQuery(id+"F8.boolean.opBoolean","MERGE",FACE,{"derivedFrom":[makeQuery(id+"F7.boolean.opBoolean","MERGE",FACE,{"derivedFrom":[makeQuery(id+"F1.opExtrude","SWEPT_FACE",FACE,{"disambiguationData":[OSD([sQuery(id+"F0.wireOp",EDGE,"E7")])]}),makeQuery(id+"F7.opExtrude","SWEPT_FACE",FACE,{"disambiguationData":[OSD([subQ2])]})]}),makeQuery(id+"F8.opExtrude","SWEPT_FACE",FACE,{"disambiguationData":[OSD([subQ2])]})]}),makeQuery(id+"F10.opExtrude","CAP_FACE",FACE,{"disambiguationData":[OSD([subQ1,sQuery(id+"F9.wireOp",EDGE,"E16"),sQuery(id+"F9.wireOp",EDGE,"E17"),subQ0,sQuery(id+"F9.wireOp",EDGE,"E19.MirrorCS"),sQuery(id+"F9.wireOp",EDGE,"E22.MirrorCS"),sQuery(id+"F9.wireOp",EDGE,"E23")])],"isStart":true})]}),makeQuery(id+"F12.opExtrude","CAP_FACE",FACE,{"disambiguationData":[OSD([subQ1,subQ0,sQuery(id+"F11.wireOp",EDGE,"E24")])],"isStart":true})]});Q0=makeQuery(id+"F28.boolean.opBoolean","MERGE",FACE,{"derivedFrom":[subQ3,makeQuery(id+"F28.opPattern","COPY",FACE,{"derivedFrom":subQ3,"instanceName":"1"})]});}
            var sketch = newSketch(context, id + "F29", { "sketchPlane" : qUnion([Q0])});
            skLineSegment(sketch, "E40", {"start": v(0, 26) * mm, "end": v(0, 0) * mm, "construction": true});
            skLineSegment(sketch, "E41.bottom", {"start": v(21, 0) * mm, "end": v(-21, 0) * mm});
            skLineSegment(sketch, "E41.top", {"start": v(21, 52) * mm, "end": v(-21, 52) * mm});
            skLineSegment(sketch, "E41.left", {"start": v(21, 0) * mm, "end": v(21, 52) * mm});
            skLineSegment(sketch, "E41.right", {"start": v(-21, 0) * mm, "end": v(-21, 52) * mm});
            skPoint(sketch, "E41.middle", {"position": v(0, 26) * mm});
            skLineSegment(sketch, "E42", {"start": v(-21, 52) * mm, "end": v(21, 10) * mm, "construction": true});
            skCircle(sketch, "E43", {"center": v(0, 31) * mm, "radius": 11.25 * mm});
            skLineSegment(sketch, "E44.bottom", {"start": v(15.5, 46.5) * mm, "end": v(-15.5, 46.5) * mm, "construction": true});
            skLineSegment(sketch, "E44.top", {"start": v(15.5, 15.5) * mm, "end": v(-15.5, 15.5) * mm, "construction": true});
            skLineSegment(sketch, "E44.left", {"start": v(15.5, 46.5) * mm, "end": v(15.5, 15.5) * mm, "construction": true});
            skLineSegment(sketch, "E44.right", {"start": v(-15.5, 46.5) * mm, "end": v(-15.5, 15.5) * mm, "construction": true});
            skCircle(sketch, "E45", {"center": v(-15.5, 15.5) * mm, "radius": 2 * mm});
            skCircle(sketch, "E46", {"center": v(-15.5, 46.5) * mm, "radius": 2 * mm});
            skCircle(sketch, "E47", {"center": v(15.5, 46.5) * mm, "radius": 2 * mm});
            skCircle(sketch, "E48", {"center": v(15.5, 15.5) * mm, "radius": 2 * mm});
            skSolve(sketch);
        }
        {
            var Q0;
            {var subQ1=sQuery(id+"F29.wireOp",EDGE,"E41.top");Q0=makeQuery(id+"F29.imprint","IMPRINT",FACE,{"disambiguationData":[TD([[makeQuery(id+"F29.imprint","IMPRINT",EDGE,{"derivedFrom":subQ1}),1.0]])]});}
            extrude(context, id + "F30", {"entities" : qUnion([Q0]), "operationType" : NewBodyOperationType.ADD, "oppositeDirection" : true, "depth" : 6 * mm, "offsetDistance" : 25 * mm});
        }
        {
            var Q0;
            Q0=makeQuery(id+"F30.opExtrude","SWEPT_FACE",FACE,{"disambiguationData":[OSD([sQuery(id+"F29.wireOp",EDGE,"E41.right")])]});
            var sketch = newSketch(context, id + "F31", { "sketchPlane" : qUnion([Q0])});
            skLineSegment(sketch, "E49", {"start": v(56, 52) * mm, "end": v(43, 10) * mm});
            skLineSegment(sketch, "E50", {"start": v(43, 10) * mm, "end": v(56, 10) * mm});
            skLineSegment(sketch, "E51", {"start": v(56, 10) * mm, "end": v(56, 52) * mm});
            skSolve(sketch);
        }
        {
            var Q0;
            Q0 = qSketchRegion(id + "F31", true);
            var Q1;
            Q1=makeQuery(id+"F31.imprint","IMPRINT",FACE,{"disambiguationData":[TD([[makeQuery(id+"F31.imprint","IMPRINT",EDGE,{"derivedFrom":sQuery(id+"F31.wireOp",EDGE,"E51")}),-1.0]])]});
            extrude(context, id + "F32", {"entities" : qUnion([Q0, Q1]), "depth" : 5 * mm, "offsetDistance" : 25 * mm});
        }
        {
            var Q0;
            Q0=makeQuery(id+"F32.opExtrude","SWEPT_BODY",BODY,{"disambiguationData":[OSD([sQuery(id+"F0.wireOp",EDGE,"E3"),sQuery(id+"F0.wireOp",EDGE,"E5"),sQuery(id+"F0.wireOp",EDGE,"E6"),sQuery(id+"F6.wireOp",EDGE,"E12.bottom"),sQuery(id+"F6.wireOp",EDGE,"E12.top"),sQuery(id+"F6.wireOp",EDGE,"E12.left"),sQuery(id+"F6.wireOp",EDGE,"E12.right"),sQuery(id+"F29.wireOp",EDGE,"E41.top"),sQuery(id+"F29.wireOp",EDGE,"E41.right"),sQuery(id+"F31.wireOp",EDGE,"E49"),sQuery(id+"F31.wireOp",EDGE,"E50")])]});
            var Q1;
            Q1=qCreatedBy(makeId("Front.planeOp"),FACE);
            mirror(context, id + "F33", {"operationType" : NewBodyOperationType.ADD, "entities" : qUnion([Q0]), "mirrorPlane" : qUnion([Q1])});
        }
        {
            var Q0;
            {var subQ1=sQuery(id+"F17.wireOp",EDGE,"E28.top");var subQ2=sQuery(id+"F3.wireOp",EDGE,"E9.5");var subQ3=makeQuery(id+"F5.opExtrude","SWEPT_FACE",FACE,{"disambiguationData":[OSD([subQ2])]});var subQ16=sQuery(id+"F0.wireOp",EDGE,"E2");var subQ17=sQuery(id+"F0.wireOp",EDGE,"E1");var subQ18=sQuery(id+"F0.wireOp",EDGE,"E0");var subQ20=sQuery(id+"F17.wireOp",EDGE,"E27.top");var subQ24=sQuery(id+"F17.wireOp",EDGE,"E28.bottom");var subQ26=makeQuery(id+"F1.opExtrude","SWEPT_FACE",FACE,{"disambiguationData":[OSD([subQ17])]});var subQ27=sQuery(id+"F17.wireOp",EDGE,"E27.bottom");var subQ28=makeQuery(id+"F1.opExtrude","SWEPT_FACE",FACE,{"disambiguationData":[OSD([subQ18])]});var subQ29=makeQuery(id+"F27.opPattern","COPY",FACE,{"derivedFrom":makeQuery(id+"F20.boolean.opBoolean","SPLIT",FACE,{"disambiguationData":[TD([makeQuery(id+"F5.boolean.opBoolean","COPY",FACE,{"derivedFrom":subQ3})])],"derivedFrom":makeQuery(id+"F18.boolean.opBoolean","MERGE",FACE,{"derivedFrom":[makeQuery(id+"F1.opExtrude","SWEPT_FACE",FACE,{"disambiguationData":[OSD([subQ16])]}),makeQuery(id+"F5.boolean.opBoolean","SPLIT",FACE,{"disambiguationData":[TD([subQ26])],"derivedFrom":makeQuery(id+"F2.boolean.opBoolean","MERGE",FACE,{"derivedFrom":[subQ28,makeQuery(id+"F2.opPattern","COPY",FACE,{"derivedFrom":subQ28,"instanceName":"1"})]})}),makeQuery(id+"F18.opExtrude","CAP_FACE",FACE,{"disambiguationData":[OSD([subQ27,subQ20,sQuery(id+"F17.wireOp",EDGE,"E27.left"),sQuery(id+"F17.wireOp",EDGE,"E27.right")])],"isStart":true}),makeQuery(id+"F18.opExtrude","CAP_FACE",FACE,{"disambiguationData":[OSD([subQ24,subQ1,sQuery(id+"F17.wireOp",EDGE,"E28.left"),sQuery(id+"F17.wireOp",EDGE,"E28.right")])],"isStart":true})]})}),"instanceName":"1"});Q0=makeQuery(id+"F28.boolean.opBoolean","MERGE",FACE,{"derivedFrom":[subQ29,makeQuery(id+"F28.opPattern","COPY",FACE,{"derivedFrom":subQ29,"instanceName":"1"})]});}
            var sketch = newSketch(context, id + "F34", { "sketchPlane" : qUnion([Q0])});
            skLineSegment(sketch, "E52", {"start": v(0, 0) * mm, "end": v(0, 9.5) * mm, "construction": true});
            skLineSegment(sketch, "E53.bottom", {"start": v(6.06, 14.5) * mm, "end": v(-6.06, 14.5) * mm});
            skLineSegment(sketch, "E53.top", {"start": v(6.06, 9.5) * mm, "end": v(-6.06, 9.5) * mm});
            skLineSegment(sketch, "E53.left", {"start": v(6.06, 14.5) * mm, "end": v(6.06, 9.5) * mm});
            skLineSegment(sketch, "E53.right", {"start": v(-6.06, 14.5) * mm, "end": v(-6.06, 9.5) * mm});
            skPoint(sketch, "E53.middle", {"position": v(0, 12) * mm});
            skLineSegment(sketch, "E54.1.0", {"start": v(-6.06, -9.5) * mm, "end": v(6.06, -9.5) * mm});
            skLineSegment(sketch, "E54.1.1", {"start": v(-6.06, -14.5) * mm, "end": v(6.06, -14.5) * mm});
            skPoint(sketch, "E54.1.2", {"position": v(0, -12) * mm});
            skLineSegment(sketch, "E54.1.3", {"start": v(-6.06, -14.5) * mm, "end": v(-6.06, -9.5) * mm});
            skLineSegment(sketch, "E54.1.4", {"start": v(6.06, -14.5) * mm, "end": v(6.06, -9.5) * mm});
            skPoint(sketch, "E54.center", {"position": v(0, 0) * mm});
            skSolve(sketch);
        }
        {
            var Q0;
            Q0 = qSketchRegion(id + "F34", true);
            var Q1;
            Q1=makeQuery(id+"F1.opExtrude","SWEPT_BODY",BODY,{"disambiguationData":[OSD([sQuery(id+"F0.wireOp",EDGE,"E0"),sQuery(id+"F0.wireOp",EDGE,"E1"),sQuery(id+"F0.wireOp",EDGE,"E2"),sQuery(id+"F0.wireOp",EDGE,"E3"),sQuery(id+"F0.wireOp",EDGE,"E4"),sQuery(id+"F0.wireOp",EDGE,"E5"),sQuery(id+"F0.wireOp",EDGE,"E6"),sQuery(id+"F0.wireOp",EDGE,"E7"),sQuery(id+"F0.wireOp",EDGE,"E8")])]});
            extrude(context, id + "F35", {"entities" : qUnion([Q0]), "operationType" : NewBodyOperationType.ADD, "endBound" : BoundingType.UP_TO_BODY, "oppositeDirection" : true, "depth" : 25 * mm, "endBoundEntityBody" : qUnion([Q1]), "offsetDistance" : 25 * mm});
        }
        {
            var Q0;
            Q0=makeQuery(id+"F35.opExtrude","SWEPT_FACE",FACE,{"disambiguationData":[OSD([sQuery(id+"F34.wireOp",EDGE,"E53.top")])]});
            var sketch = newSketch(context, id + "F36", { "sketchPlane" : qUnion([Q0])});
            skCircle(sketch, "E55", {"center": v(0, 0) * mm, "radius": 3.5 * mm});
            skSolve(sketch);
        }
        {
            var Q0;
            {var subQ0=sQuery(id+"F36.wireOp",EDGE,"E55");var subQ1=makeQuery(id+"F35.opExtrude","CAP_EDGE",EDGE,{"disambiguationData":[OSD([sQuery(id+"F34.wireOp",EDGE,"E53.top")])],"isStart":true});var subQ2=makeQuery(id+"F36.imprint","INTERSECT",VERTEX,{"disambiguationData":[OD(0.0)],"derivedFrom":[subQ1,subQ0]});Q0=makeQuery(id+"F36.imprint","IMPRINT",FACE,{"disambiguationData":[TD([[makeQuery(id+"F36.imprint","IMPRINT",EDGE,{"disambiguationData":[TD([[subQ2,1.0]])],"derivedFrom":subQ0}),1.0]])]});}
            extrude(context, id + "F37", {"entities" : qUnion([Q0]), "operationType" : NewBodyOperationType.REMOVE, "endBound" : BoundingType.SYMMETRIC, "oppositeDirection" : true, "depth" : 1000 * mm, "offsetDistance" : 25 * mm});
        }
        {
            var Q0;
            {var subQ0=sQuery(id+"F0.wireOp",EDGE,"E3");var subQ5=sQuery(id+"F0.wireOp",EDGE,"E4");var subQ17=makeQuery(id+"F1.opExtrude","SWEPT_FACE",FACE,{"disambiguationData":[OSD([subQ5])]});var subQ18=makeQuery(id+"F4.boolean.opBoolean","SPLIT",FACE,{"disambiguationData":[TD([makeQuery(id+"F1.opExtrude","SWEPT_FACE",FACE,{"disambiguationData":[OSD([subQ0])]})])],"derivedFrom":makeQuery(id+"F2.boolean.opBoolean","MERGE",FACE,{"derivedFrom":[subQ17,makeQuery(id+"F2.opPattern","COPY",FACE,{"derivedFrom":subQ17,"instanceName":"1"})]})});Q0=makeQuery(id+"F28.boolean.opBoolean","MERGE",FACE,{"derivedFrom":[subQ18,makeQuery(id+"F28.opPattern","COPY",FACE,{"derivedFrom":subQ18,"instanceName":"1"})]});}
            var sketch = newSketch(context, id + "F38", { "sketchPlane" : qUnion([Q0])});
            skLineSegment(sketch, "E56", {"start": v(0, 0) * mm, "end": v(-8.5, 0) * mm, "construction": true});
            skPoint(sketch, "E56.endSnap0", {"position": v(-7.5, 0) * mm});
            skLineSegment(sketch, "E57.bottom", {"start": v(-7.5, 2) * mm, "end": v(-9.5, 2) * mm});
            skLineSegment(sketch, "E57.top", {"start": v(-7.5, -2) * mm, "end": v(-9.5, -2) * mm});
            skLineSegment(sketch, "E57.left", {"start": v(-7.5, 2) * mm, "end": v(-7.5, -2) * mm});
            skLineSegment(sketch, "E57.right", {"start": v(-9.5, 2) * mm, "end": v(-9.5, -2) * mm});
            skPoint(sketch, "E57.middle", {"position": v(-8.5, 0) * mm});
            skPoint(sketch, "E58.1.0", {"position": v(8.5, 0) * mm});
            skPoint(sketch, "E58.1.1", {"position": v(7.5, 0) * mm});
            skLineSegment(sketch, "E58.1.2", {"start": v(7.5, 2) * mm, "end": v(9.5, 2) * mm});
            skLineSegment(sketch, "E58.1.3", {"start": v(7.5, -2) * mm, "end": v(7.5, 2) * mm});
            skLineSegment(sketch, "E58.1.4", {"start": v(7.5, -2) * mm, "end": v(9.5, -2) * mm});
            skLineSegment(sketch, "E58.1.5", {"start": v(9.5, -2) * mm, "end": v(9.5, 2) * mm});
            skPoint(sketch, "E58.center", {"position": v(0, 0) * mm});
            skSolve(sketch);
        }
        {
            var Q0;
            Q0 = qSketchRegion(id + "F38", true);
            extrude(context, id + "F39", {"entities" : qUnion([Q0]), "operationType" : NewBodyOperationType.REMOVE, "endBound" : BoundingType.THROUGH_ALL, "oppositeDirection" : true, "depth" : 25 * mm, "offsetDistance" : 25 * mm});
        }
    });
